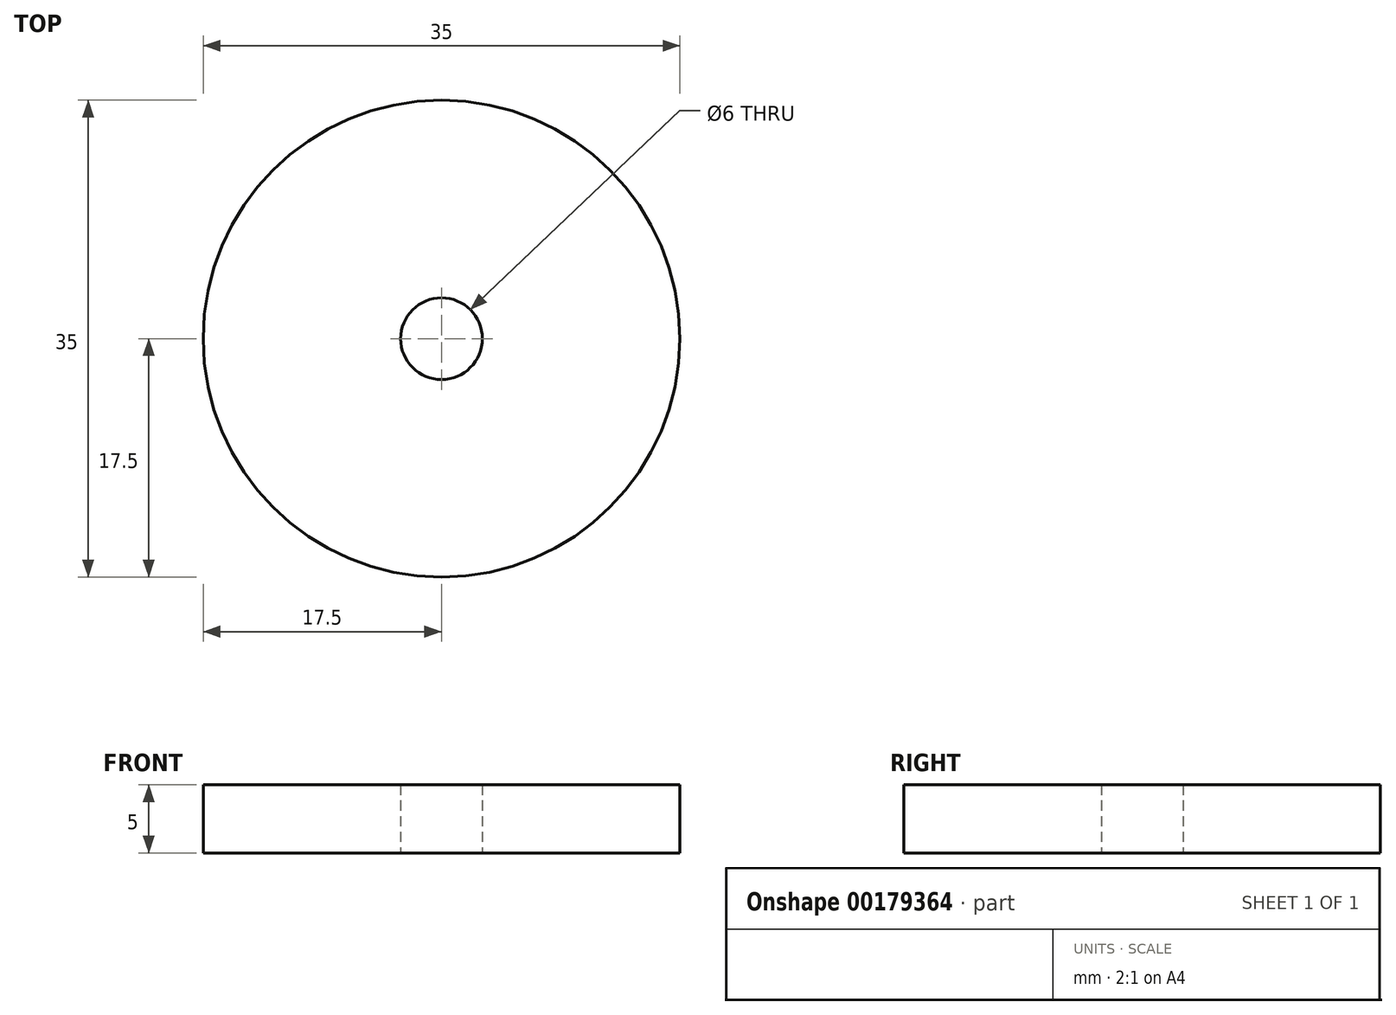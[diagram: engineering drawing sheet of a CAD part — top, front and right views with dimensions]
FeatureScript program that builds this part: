
annotation { "Feature Type Name" : "Feature", "Feature Type Description" : "" }
export const myFeature = defineFeature(function(context is Context, id is Id, definition is map)
    precondition{}
    {
        {
            var Q0;
            Q0=qCreatedBy(makeId("Top.planeOp"),FACE);
            var sketch = newSketch(context, id + "F0", { "sketchPlane" : qUnion([Q0])});
            skCircle(sketch, "E0", {"center": v(0, 0) * mm, "radius": 17.5 * mm});
            skCircle(sketch, "E1", {"center": v(0, 0) * mm, "radius": 3 * mm});
            skSolve(sketch);
        }
        {
            var Q0;
            Q0 = qSketchRegion(id + "F0", true);
            extrude(context, id + "F1", {"entities" : qUnion([Q0]), "depth" : 5 * mm, "offsetDistance" : 25 * mm});
        }
    });
